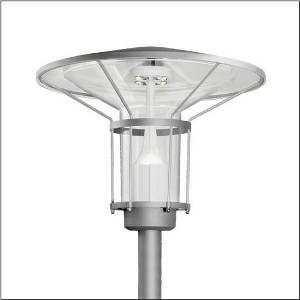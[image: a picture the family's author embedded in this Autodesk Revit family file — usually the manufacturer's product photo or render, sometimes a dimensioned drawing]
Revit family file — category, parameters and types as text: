
# Revit family: laterne_classic_iq___st1_2a_5xa5245ef14h000022_520b
name_source: partatom
category: Lighting Fixtures
units: mm (PartAtom-declared; Revit-internal decimal feet)

## family parameters
Cut with Voids When Loaded = No
Host = Face
Light Source = No
Part Type = Normal
Room Calculation Point = No
Round Connector Dimension = Use Diameter
Shared = No

## types (1)
- --- (1 x LED, 1380 lm, 10.5 W, 3000K)
    Apparent Load = 11 VA
    CIE Flux Codes = 21 60 93 97 100
    Color Rendering = 70
    Color Temperature = 3000K
    Default Elevation = 1800 mm
    Description = Lantern Classic iQ, mast luminaire, Module 540 iQ-SR, primary light control with 3 zone facetted reflector, of plastic, silver coated, highly specular, structured, primary optical cover: cover, of PMMA, transparent, light distribution: ST1.2a, light emission: direct distribution, primary light characteristic: asymmetric, installation type: post-top, LED, High Power LED, rated luminous flux: 1.380lm, luminous efficacy: 131lm/W, light colour: 730, colour temperature: 3000K, control gear: iQ Street-Remote, control: Street-Remote, Auto-Match, Temp-Guard, Lumen-Switch, Night-Set, Smart-Wire, Light-Fading, Desk-Remote (wireless, voltage-free reading and setting of iQ features in the workshop via application-optimized NFC function/RFID function), optimised constant luminous flux control (CLO 2.0), pre-setting: logarithmic dimming characteristic, mains connection: 230..240V, AC, 50/60Hz, connection cable pre-assembled, cable length: 5,5m, wiring characteristics: H07RN-F, start of lifetime: 11W, end of service life: 11W, reduction: 5W, luminaire housing, upper part, of glass-fibre reinforced polyester, coated, Siteco® metallic grey (DB 702S), diameter: 750mm, height: 596mm, spigot size: d x l = 76 x 70mm (post-top) | with reducer (optional accessory) 60 x 70mm, mounting height: 3..5m, post-top mast mounting element, of diecast aluminium, coated, Siteco® metallic grey (DB 702S), Module 540 iQ-SR, traffic white (RAL 9016), equipment: standard, protection rating (complete): IP65, insulation class (complete): insulation class II (safety insulation), certification: CE, ENEC, VDE, packaging unit: 1 piece

Light Distribution: ST1.2a
    Height = 596 mm
    Lamp = 1 x LED
    Lamp Light Flux = 1380 lm
    Lamp Power = 10.5 W
    Lamp count = 1
    Length = 750 mm
    Luminous efficacy = 131 lm/W
    Manufacturer = Siteco
    ModVariant = No
    Model = 5XA5245EF14H000022
    Number of Poles = 1
    OnlyDefault = Yes
    Power Factor = 1
    Product Name = Laterne Classic iQ | ST1.2a
    Product group = mast luminaire | pylon top
    ProductGroupID = 6100
    Protection Class = Protection class II
    Protection Degree = IP 65
    RLX_Detail_Level = 1
    RLX_Emergency_Light_Flux = 0 lm
    RLX_Emergency_Type = 0
    RLX_Emergency_Type_DB = No
    RlxData = <blob elided: 39377 chars, md5=1ae555d0>
    Socket = socket
    Standby Power = 0 W
    System Light Flux = 1380 lm
    System Power = 11 W
    Type Comments = factory setting: luminous flux: 100 % | dim-lin: 254 | 419 mA
    Type Image = l_1006052.jpg
    URL = http://relux.com
    VarID = @adj_181777
    Voltage = 0 V
    Weight = 0.00 kg
    Width = 0 mm  [stored 0 ft]

note: [stored X ft] marks values corroborated as IEEE doubles in the binary element streams (Revit-internal decimal feet)

## geometry (parser evidence)
native form markers: Blend x4, Sweep x11
no freeform markers — native parametric forms only
